# Revit family: Plastic-Components_Ultra-Trac-Intersection_Cross-Intersection
name_source: partatom
category: Generic Models
units: mm (PartAtom-declared; Revit-internal decimal feet)

## family parameters
Always vertical = No
Can host rebar = No
Cut with Voids When Loaded = No
Maintain Annotation Orientation = No
Part Type = Normal
Room Calculation Point = No
Round Connector Dimension = Use Diameter
Shared = No
Work Plane-Based = Yes

## types (1)
- Plastic-Components_Ultra-Trac-Intersection_Cross-Intersection
    Assembly Code = C3020800
    Construction Details = http://www.arcat.com
    Default Elevation = 4' - 0"
    Expected Lifespan (Years) = 0
    Green Building-LEED = http://www.arcat.com
    Installation Phase = Stucco Underlayment
    Installation-Fabrication = http://www.plasticomponents.com
    Keynote = 09 22 36
    Maintenance Schedule (Months) = 0
    Manufacturer = Plastic Components, Inc.
    Manufacturer Fax = 305-887-2452
    Manufacturer Website = www.plasticcomponents.com
    Material = Plastic Components - PVC
    Opening Width = 0' - 1"
    Product Data = http://www.arcat.com
    Product Properties = http://www.plasticomponents.com
    Revision = R1_11-2014
    Sales Information = http://www.plasticomponents.com
    Specification = http://www.arcat.com
    Test Data = http://www.plasticomponents.com
    URL = www.plasticcomponents.com
    Unit Depth = 0' - 0 3/4"
    Warranty Duration (Years) = 0

## geometry (parser evidence)
native form markers: Blend x1, Sweep x2
no freeform markers — native parametric forms only
